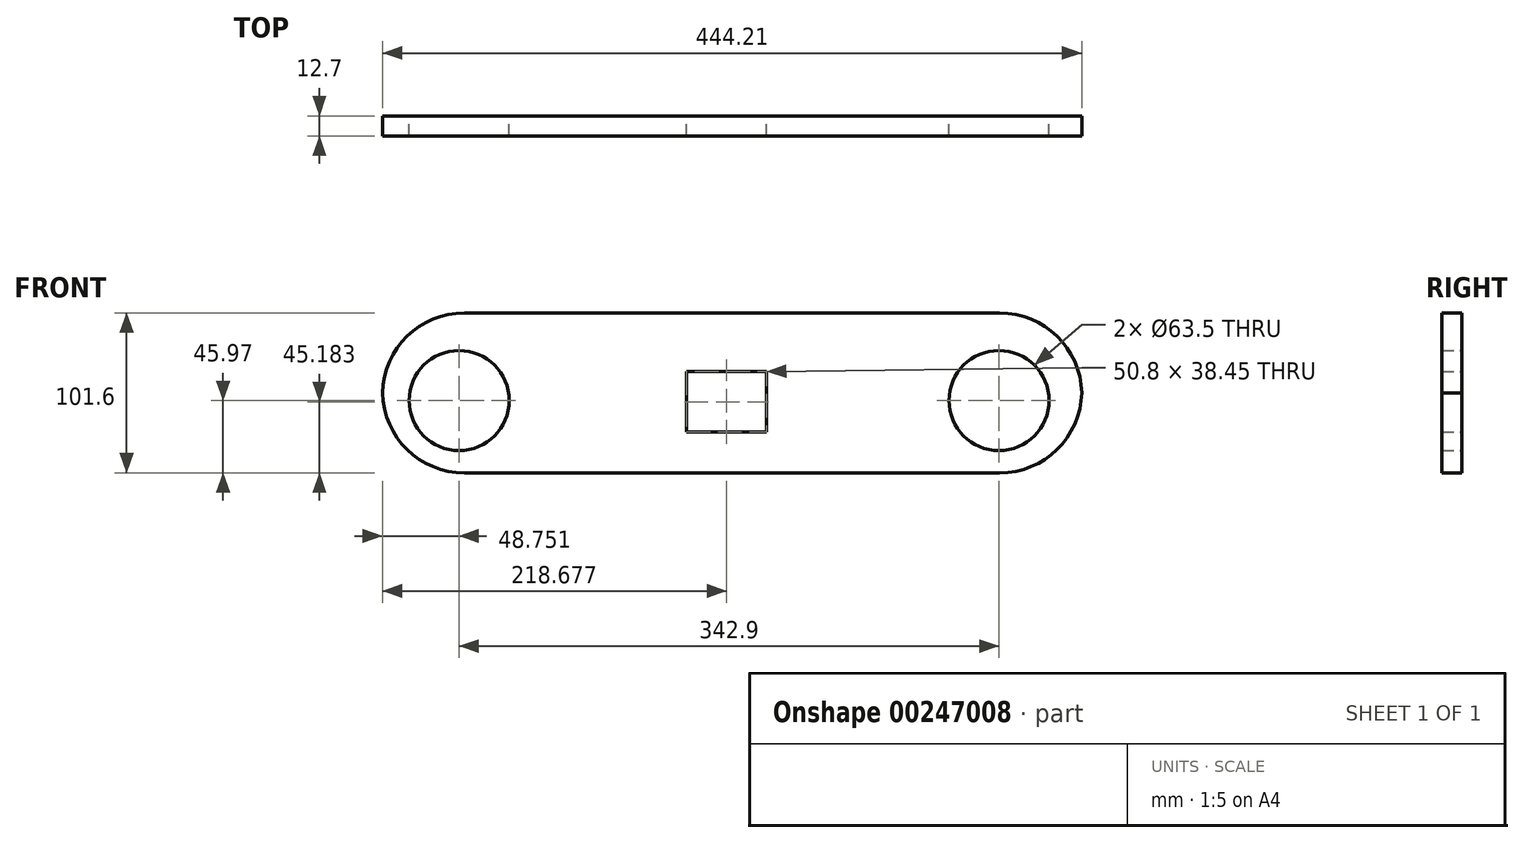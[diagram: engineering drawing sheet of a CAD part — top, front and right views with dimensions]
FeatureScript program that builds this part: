
annotation { "Feature Type Name" : "Feature", "Feature Type Description" : "" }
export const myFeature = defineFeature(function(context is Context, id is Id, definition is map)
    precondition{}
    {
        {
            var Q0;
            Q0=qCreatedBy(makeId("Front.planeOp"),FACE);
            var sketch = newSketch(context, id + "F0", { "sketchPlane" : qUnion([Q0])});
            skLineSegment(sketch, "E0", {"start": v(-196.08, 55.63) * mm, "end": v(248.16, 55.63) * mm});
            skLineSegment(sketch, "E1", {"start": v(248.16, 55.63) * mm, "end": v(248.16, -45.97) * mm});
            skLineSegment(sketch, "E2", {"start": v(248.16, -45.97) * mm, "end": v(-196.09, -45.97) * mm});
            skLineSegment(sketch, "E3", {"start": v(-196.09, -45.97) * mm, "end": v(-196.08, 55.63) * mm});
            skCircle(sketch, "E4", {"center": v(-147.32, 0) * mm, "radius": 31.75 * mm});
            skCircle(sketch, "E5", {"center": v(195.58, 0) * mm, "radius": 31.75 * mm});
            skLineSegment(sketch, "E6.bottom", {"start": v(-2.8, 18.44) * mm, "end": v(48, 18.44) * mm});
            skLineSegment(sketch, "E6.top", {"start": v(-2.8, -20.01) * mm, "end": v(48, -20.01) * mm});
            skLineSegment(sketch, "E6.left", {"start": v(-2.8, 18.44) * mm, "end": v(-2.8, -20.01) * mm});
            skLineSegment(sketch, "E6.right", {"start": v(48, 18.44) * mm, "end": v(48, -20.01) * mm});
            skSolve(sketch);
        }
        {
            var Q0;
            Q0 = qSketchRegion(id + "F0", true);
            extrude(context, id + "F1", {"entities" : qUnion([Q0]), "depth" : 12.7 * mm});
        }
        {
            var Q0;
            Q0=makeQuery(id+"F1.opExtrude","SWEPT_EDGE",EDGE,{"disambiguationData":[OSD([sQuery(id+"F0.wireOp",EDGE,"E0"),sQuery(id+"F0.wireOp",EDGE,"E1")])]});
            var Q1;
            Q1=makeQuery(id+"F1.opExtrude","SWEPT_EDGE",EDGE,{"disambiguationData":[OSD([sQuery(id+"F0.wireOp",EDGE,"E1"),sQuery(id+"F0.wireOp",EDGE,"E2")])]});
            var Q2;
            Q2=makeQuery(id+"F1.opExtrude","SWEPT_EDGE",EDGE,{"disambiguationData":[OSD([sQuery(id+"F0.wireOp",EDGE,"E0"),sQuery(id+"F0.wireOp",EDGE,"E3")])]});
            var Q3;
            Q3=makeQuery(id+"F1.opExtrude","SWEPT_EDGE",EDGE,{"disambiguationData":[OSD([sQuery(id+"F0.wireOp",EDGE,"E2"),sQuery(id+"F0.wireOp",EDGE,"E3")])]});
            fillet(context, id + "F2", {"entities" : qUnion([Q0, Q1, Q2, Q3]), "radius" : 52.12 * mm, "tangentPropagation" : true, "allowEdgeOverflow" : false});
        }
    });
